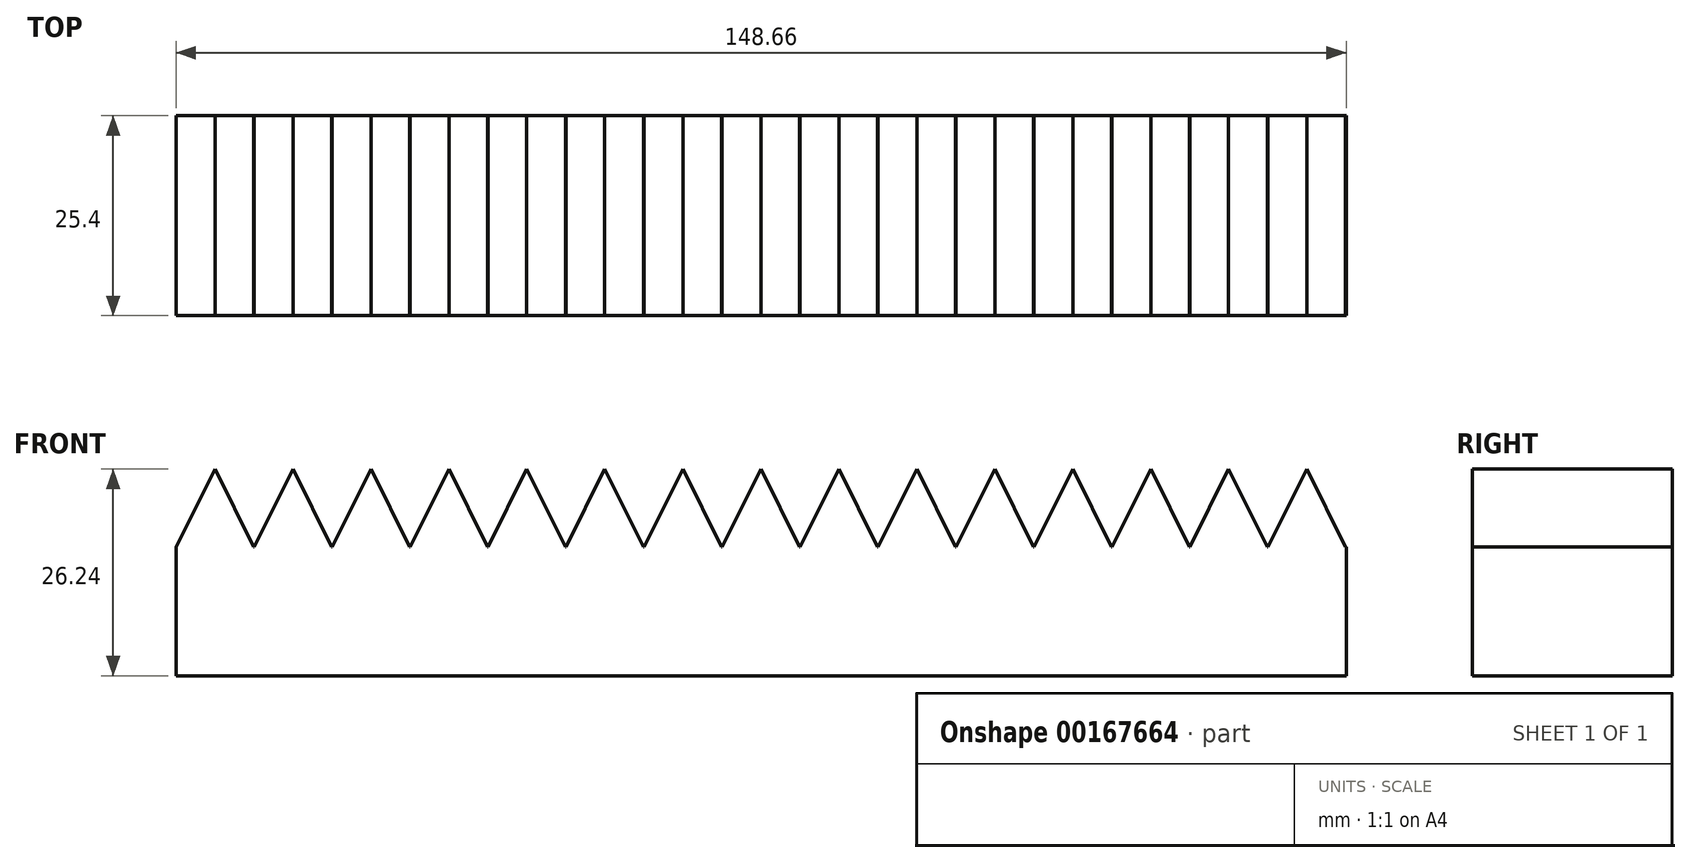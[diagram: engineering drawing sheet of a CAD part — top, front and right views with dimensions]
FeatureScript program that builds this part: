
annotation { "Feature Type Name" : "Feature", "Feature Type Description" : "" }
export const myFeature = defineFeature(function(context is Context, id is Id, definition is map)
    precondition{}
    {
        {
            var Q0;
            Q0=qCreatedBy(makeId("Front.planeOp"),FACE);
            var sketch = newSketch(context, id + "F0", { "sketchPlane" : qUnion([Q0])});
            skLineSegment(sketch, "E0", {"start": v(-64.44, 0) * mm, "end": v(-59.5, 9.9) * mm});
            skLineSegment(sketch, "E1", {"start": v(-64.44, 0) * mm, "end": v(-54.56, 0) * mm});
            skLineSegment(sketch, "E2", {"start": v(-59.5, 9.9) * mm, "end": v(-54.56, 0) * mm});
            skPoint(sketch, "E3", {"position": v(-59.5, 0) * mm});
            skLineSegment(sketch, "E4.1.0.0", {"start": v(-54.53, 0) * mm, "end": v(-49.6, 9.9) * mm});
            skLineSegment(sketch, "E4.1.0.1", {"start": v(-49.6, 9.9) * mm, "end": v(-44.65, 0) * mm});
            skLineSegment(sketch, "E4.1.0.2", {"start": v(-54.53, 0) * mm, "end": v(-44.65, 0) * mm});
            skLineSegment(sketch, "E4.2.0.0", {"start": v(-44.63, 0) * mm, "end": v(-39.69, 9.9) * mm});
            skLineSegment(sketch, "E4.2.0.1", {"start": v(-39.69, 9.9) * mm, "end": v(-34.75, 0) * mm});
            skLineSegment(sketch, "E4.2.0.2", {"start": v(-44.63, 0) * mm, "end": v(-34.75, 0) * mm});
            skLineSegment(sketch, "E4.3.0.0", {"start": v(-34.72, 0) * mm, "end": v(-29.78, 9.9) * mm});
            skLineSegment(sketch, "E4.3.0.1", {"start": v(-29.78, 9.9) * mm, "end": v(-24.84, 0) * mm});
            skLineSegment(sketch, "E4.3.0.2", {"start": v(-34.72, 0) * mm, "end": v(-24.84, 0) * mm});
            skLineSegment(sketch, "E4.4.0.0", {"start": v(-24.81, 0) * mm, "end": v(-19.87, 9.9) * mm});
            skLineSegment(sketch, "E4.4.0.1", {"start": v(-19.87, 9.9) * mm, "end": v(-14.93, 0) * mm});
            skLineSegment(sketch, "E4.4.0.2", {"start": v(-24.81, 0) * mm, "end": v(-14.93, 0) * mm});
            skLineSegment(sketch, "E4.5.0.0", {"start": v(-14.9, 0) * mm, "end": v(-9.97, 9.9) * mm});
            skLineSegment(sketch, "E4.5.0.1", {"start": v(-9.97, 9.9) * mm, "end": v(-5.03, 0) * mm});
            skLineSegment(sketch, "E4.5.0.2", {"start": v(-14.9, 0) * mm, "end": v(-5.03, 0) * mm});
            skLineSegment(sketch, "E4.6.0.0", {"start": v(-5, 0) * mm, "end": v(-0.06, 9.9) * mm});
            skLineSegment(sketch, "E4.6.0.1", {"start": v(-0.06, 9.9) * mm, "end": v(4.88, 0) * mm});
            skLineSegment(sketch, "E4.6.0.2", {"start": v(-5, 0) * mm, "end": v(4.88, 0) * mm});
            skLineSegment(sketch, "E4.7.0.0", {"start": v(4.9, 0) * mm, "end": v(9.84, 9.9) * mm});
            skLineSegment(sketch, "E4.7.0.1", {"start": v(9.84, 9.9) * mm, "end": v(14.78, 0) * mm});
            skLineSegment(sketch, "E4.7.0.2", {"start": v(4.9, 0) * mm, "end": v(14.78, 0) * mm});
            skLineSegment(sketch, "E4.8.0.0", {"start": v(14.8, 0) * mm, "end": v(19.75, 9.9) * mm});
            skLineSegment(sketch, "E4.8.0.1", {"start": v(19.75, 9.9) * mm, "end": v(24.69, 0) * mm});
            skLineSegment(sketch, "E4.8.0.2", {"start": v(14.8, 0) * mm, "end": v(24.69, 0) * mm});
            skLineSegment(sketch, "E4.9.0.0", {"start": v(24.72, 0) * mm, "end": v(29.66, 9.9) * mm});
            skLineSegment(sketch, "E4.9.0.1", {"start": v(29.66, 9.9) * mm, "end": v(34.6, 0) * mm});
            skLineSegment(sketch, "E4.9.0.2", {"start": v(24.72, 0) * mm, "end": v(34.6, 0) * mm});
            skLineSegment(sketch, "E4.10.0.0", {"start": v(34.62, 0) * mm, "end": v(39.56, 9.9) * mm});
            skLineSegment(sketch, "E4.10.0.1", {"start": v(39.56, 9.9) * mm, "end": v(44.5, 0) * mm});
            skLineSegment(sketch, "E4.10.0.2", {"start": v(34.62, 0) * mm, "end": v(44.5, 0) * mm});
            skLineSegment(sketch, "E4.11.0.0", {"start": v(44.53, 0) * mm, "end": v(49.47, 9.9) * mm});
            skLineSegment(sketch, "E4.11.0.1", {"start": v(49.47, 9.9) * mm, "end": v(54.4, 0) * mm});
            skLineSegment(sketch, "E4.11.0.2", {"start": v(44.53, 0) * mm, "end": v(54.4, 0) * mm});
            skLineSegment(sketch, "E4.12.0.0", {"start": v(54.43, 0) * mm, "end": v(59.37, 9.9) * mm});
            skLineSegment(sketch, "E4.12.0.1", {"start": v(59.37, 9.9) * mm, "end": v(64.31, 0) * mm});
            skLineSegment(sketch, "E4.12.0.2", {"start": v(54.43, 0) * mm, "end": v(64.31, 0) * mm});
            skLineSegment(sketch, "E4.13.0.0", {"start": v(64.34, 0) * mm, "end": v(69.28, 9.9) * mm});
            skLineSegment(sketch, "E4.13.0.1", {"start": v(69.28, 9.9) * mm, "end": v(74.22, 0) * mm});
            skLineSegment(sketch, "E4.13.0.2", {"start": v(64.34, 0) * mm, "end": v(74.22, 0) * mm});
            skLineSegment(sketch, "E4.14.0.0", {"start": v(74.25, 0) * mm, "end": v(79.19, 9.9) * mm});
            skLineSegment(sketch, "E4.14.0.1", {"start": v(79.19, 9.9) * mm, "end": v(84.13, 0) * mm});
            skLineSegment(sketch, "E4.14.0.2", {"start": v(74.25, 0) * mm, "end": v(84.13, 0) * mm});
            skLineSegment(sketch, "E4.direction1", {"start": v(-64.44, 0) * mm, "end": v(-54.53, 0) * mm, "construction": true});
            skLineSegment(sketch, "E5.bottom", {"start": v(-64.44, 0) * mm, "end": v(84.22, 0) * mm});
            skLineSegment(sketch, "E5.top", {"start": v(-64.44, -16.35) * mm, "end": v(84.22, -16.35) * mm});
            skLineSegment(sketch, "E5.left", {"start": v(-64.44, 0) * mm, "end": v(-64.44, -16.35) * mm});
            skLineSegment(sketch, "E5.right", {"start": v(84.22, 0) * mm, "end": v(84.22, -16.35) * mm});
            skSolve(sketch);
        }
        {
            var Q0;
            {var subQ0=sQuery(id+"F0.wireOp",EDGE,"E4.12.0.0");Q0=makeQuery(id+"F0.imprint","IMPRINT",FACE,{"disambiguationData":[TD([[makeQuery(id+"F0.imprint","IMPRINT",EDGE,{"derivedFrom":subQ0}),-1.0]])]});}
            var Q1;
            {var subQ0=sQuery(id+"F0.wireOp",EDGE,"E4.11.0.0");Q1=makeQuery(id+"F0.imprint","IMPRINT",FACE,{"disambiguationData":[TD([[makeQuery(id+"F0.imprint","IMPRINT",EDGE,{"derivedFrom":subQ0}),-1.0]])]});}
            var Q2;
            {var subQ0=sQuery(id+"F0.wireOp",EDGE,"E4.10.0.0");Q2=makeQuery(id+"F0.imprint","IMPRINT",FACE,{"disambiguationData":[TD([[makeQuery(id+"F0.imprint","IMPRINT",EDGE,{"derivedFrom":subQ0}),-1.0]])]});}
            var Q3;
            {var subQ0=sQuery(id+"F0.wireOp",EDGE,"E4.9.0.0");Q3=makeQuery(id+"F0.imprint","IMPRINT",FACE,{"disambiguationData":[TD([[makeQuery(id+"F0.imprint","IMPRINT",EDGE,{"derivedFrom":subQ0}),-1.0]])]});}
            var Q4;
            {var subQ0=sQuery(id+"F0.wireOp",EDGE,"E4.8.0.0");Q4=makeQuery(id+"F0.imprint","IMPRINT",FACE,{"disambiguationData":[TD([[makeQuery(id+"F0.imprint","IMPRINT",EDGE,{"derivedFrom":subQ0}),-1.0]])]});}
            var Q5;
            {var subQ0=sQuery(id+"F0.wireOp",EDGE,"E4.7.0.0");Q5=makeQuery(id+"F0.imprint","IMPRINT",FACE,{"disambiguationData":[TD([[makeQuery(id+"F0.imprint","IMPRINT",EDGE,{"derivedFrom":subQ0}),-1.0]])]});}
            var Q6;
            {var subQ0=sQuery(id+"F0.wireOp",EDGE,"E4.6.0.0");Q6=makeQuery(id+"F0.imprint","IMPRINT",FACE,{"disambiguationData":[TD([[makeQuery(id+"F0.imprint","IMPRINT",EDGE,{"derivedFrom":subQ0}),-1.0]])]});}
            var Q7;
            {var subQ0=sQuery(id+"F0.wireOp",EDGE,"E4.5.0.0");Q7=makeQuery(id+"F0.imprint","IMPRINT",FACE,{"disambiguationData":[TD([[makeQuery(id+"F0.imprint","IMPRINT",EDGE,{"derivedFrom":subQ0}),-1.0]])]});}
            var Q8;
            {var subQ0=sQuery(id+"F0.wireOp",EDGE,"E4.4.0.0");Q8=makeQuery(id+"F0.imprint","IMPRINT",FACE,{"disambiguationData":[TD([[makeQuery(id+"F0.imprint","IMPRINT",EDGE,{"derivedFrom":subQ0}),-1.0]])]});}
            var Q9;
            {var subQ0=sQuery(id+"F0.wireOp",EDGE,"E4.3.0.0");Q9=makeQuery(id+"F0.imprint","IMPRINT",FACE,{"disambiguationData":[TD([[makeQuery(id+"F0.imprint","IMPRINT",EDGE,{"derivedFrom":subQ0}),-1.0]])]});}
            var Q10;
            {var subQ0=sQuery(id+"F0.wireOp",EDGE,"E4.2.0.0");Q10=makeQuery(id+"F0.imprint","IMPRINT",FACE,{"disambiguationData":[TD([[makeQuery(id+"F0.imprint","IMPRINT",EDGE,{"derivedFrom":subQ0}),-1.0]])]});}
            var Q11;
            {var subQ0=sQuery(id+"F0.wireOp",EDGE,"E4.1.0.0");Q11=makeQuery(id+"F0.imprint","IMPRINT",FACE,{"disambiguationData":[TD([[makeQuery(id+"F0.imprint","IMPRINT",EDGE,{"derivedFrom":subQ0}),-1.0]])]});}
            var Q12;
            {var subQ0=sQuery(id+"F0.wireOp",EDGE,"E0");Q12=makeQuery(id+"F0.imprint","IMPRINT",FACE,{"disambiguationData":[TD([[makeQuery(id+"F0.imprint","IMPRINT",EDGE,{"derivedFrom":subQ0}),-1.0]])]});}
            var Q13;
            {var subQ0=sQuery(id+"F0.wireOp",EDGE,"E4.14.0.0");Q13=makeQuery(id+"F0.imprint","IMPRINT",FACE,{"disambiguationData":[TD([[makeQuery(id+"F0.imprint","IMPRINT",EDGE,{"derivedFrom":subQ0}),-1.0]])]});}
            var Q14;
            {var subQ0=sQuery(id+"F0.wireOp",EDGE,"E4.13.0.0");Q14=makeQuery(id+"F0.imprint","IMPRINT",FACE,{"disambiguationData":[TD([[makeQuery(id+"F0.imprint","IMPRINT",EDGE,{"derivedFrom":subQ0}),-1.0]])]});}
            var Q15;
            Q15=makeQuery(id+"F0.imprint","IMPRINT",FACE,{"disambiguationData":[TD([[makeQuery(id+"F0.imprint","IMPRINT",EDGE,{"derivedFrom":sQuery(id+"F0.wireOp",EDGE,"E5.top")}),1.0]])]});
            extrude(context, id + "F1", {"entities" : qUnion([Q0, Q1, Q2, Q3, Q4, Q5, Q6, Q7, Q8, Q9, Q10, Q11, Q12, Q13, Q14, Q15]), "depth" : 25.4 * mm});
        }
    });
